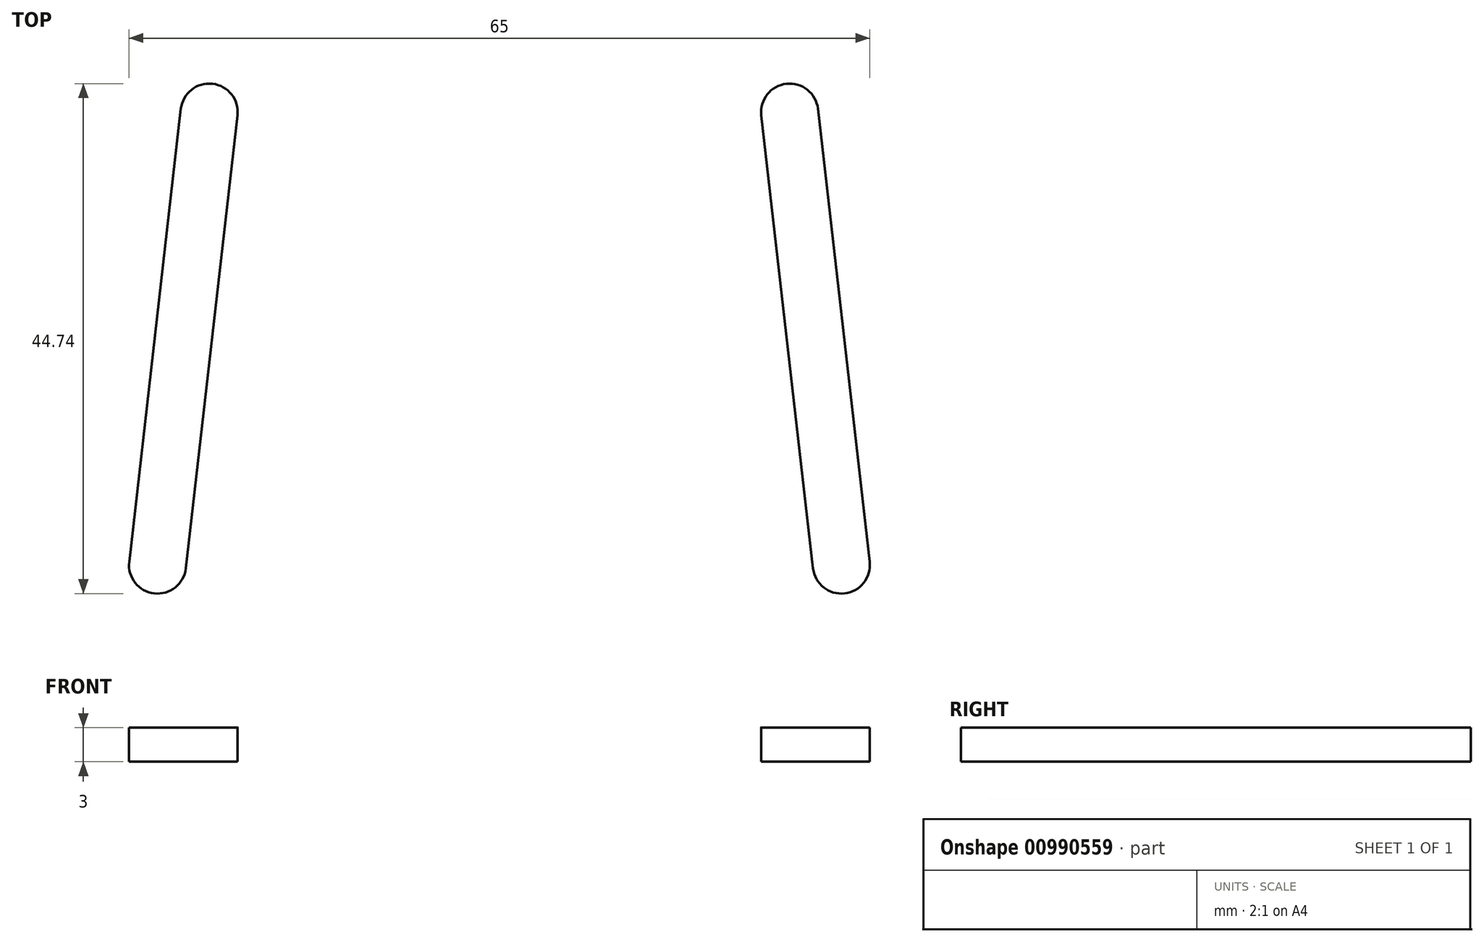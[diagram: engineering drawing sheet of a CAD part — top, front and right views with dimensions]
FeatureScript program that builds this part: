
annotation { "Feature Type Name" : "Feature", "Feature Type Description" : "" }
export const myFeature = defineFeature(function(context is Context, id is Id, definition is map)
    precondition{}
    {
        {
            var Q0;
            Q0=qCreatedBy(makeId("Top.planeOp"),FACE);
            var sketch = newSketch(context, id + "F0", { "sketchPlane" : qUnion([Q0])});
            skLineSegment(sketch, "E0.bottom", {"start": v(0, 0) * mm, "end": v(40, 0) * mm});
            skLineSegment(sketch, "E0.top", {"start": v(0, 100) * mm, "end": v(40, 100) * mm});
            skLineSegment(sketch, "E0.left", {"start": v(0, 0) * mm, "end": v(0, 100) * mm});
            skLineSegment(sketch, "E0.right", {"start": v(40, 0) * mm, "end": v(40, 100) * mm});
            skSolve(sketch);
        }
        {
            var Q0;
            Q0=makeQuery(id+"F0.imprint","IMPRINT",FACE,{"disambiguationData":[TD([[makeQuery(id+"F0.imprint","IMPRINT",EDGE,{"derivedFrom":sQuery(id+"F0.wireOp",EDGE,"E0.bottom")}),1.0]])]});
            extrude(context, id + "F1", {"entities" : qUnion([Q0]), "depth" : 3 * mm, "offsetDistance" : 25 * mm});
        }
        {
            var Q0;
            Q0=makeQuery(id+"F1.opExtrude","CAP_FACE",FACE,{"disambiguationData":[OSD([sQuery(id+"F0.wireOp",EDGE,"E0.bottom"),sQuery(id+"F0.wireOp",EDGE,"E0.top"),sQuery(id+"F0.wireOp",EDGE,"E0.left"),sQuery(id+"F0.wireOp",EDGE,"E0.right")])],"isStart":false});
            var sketch = newSketch(context, id + "F2", { "sketchPlane" : qUnion([Q0])});
            skSolve(sketch);
        }
        {
            var Q0;
            Q0=makeQuery(id+"F2.imprint","IMPRINT",FACE,{"disambiguationData":[TD([[makeQuery(id+"F2.imprint","IMPRINT",EDGE,{"derivedFrom":makeQuery(id+"F1.opExtrude","CAP_EDGE",EDGE,{"disambiguationData":[OSD([sQuery(id+"F0.wireOp",EDGE,"E0.bottom")])],"isStart":false})}),1.0]])]});
            var sketch = newSketch(context, id + "F3", { "sketchPlane" : qUnion([Q0])});
            skLineSegment(sketch, "E1", {"start": v(20, 50) * mm, "end": v(20, 25) * mm});
            skSolve(sketch);
        }
        {
            var Q0;
            Q0=sQuery(id+"F3.wireOp",VERTEX,"E1.start");
            var Q1;
            Q1=sQuery(id+"F3.wireOp",VERTEX,"E1.end");
            var Q2;
            Q2=makeQuery(id+"F1.opExtrude","SWEPT_BODY",BODY,{"disambiguationData":[OSD([sQuery(id+"F0.wireOp",EDGE,"E0.bottom"),sQuery(id+"F0.wireOp",EDGE,"E0.top"),sQuery(id+"F0.wireOp",EDGE,"E0.left"),sQuery(id+"F0.wireOp",EDGE,"E0.right")])]});
            hole(context, id + "F4", {"style" : HoleStyle.SIMPLE, "endStyle" : HoleEndStyle.THROUGH, "holeDiameter" : 3 * mm, "majorDiameter" : 5 * mm, "isTappedThrough" : true, "tappedDepth" : 12 * mm, "tapClearance" : 3, "locations" : qUnion([Q0, Q1]), "scope" : qUnion([Q2])});
        }
        {
            var Q0;
            Q0=makeQuery(id+"F2.imprint","IMPRINT",FACE,{"disambiguationData":[TD([[makeQuery(id+"F2.imprint","IMPRINT",EDGE,{"derivedFrom":makeQuery(id+"F1.opExtrude","CAP_EDGE",EDGE,{"disambiguationData":[OSD([sQuery(id+"F0.wireOp",EDGE,"E0.bottom")])],"isStart":false})}),1.0]])]});
            var sketch = newSketch(context, id + "F5", { "sketchPlane" : qUnion([Q0])});
            skLineSegment(sketch, "E2", {"start": v(30, 20) * mm, "end": v(25.46, 59.74) * mm});
            skSolve(sketch);
        }
        {
            var Q0;
            Q0=makeQuery(id+"F5.imprint","IMPRINT",FACE,{"disambiguationData":[TD([[makeQuery(id+"F5.imprint","IMPRINT",EDGE,{"derivedFrom":makeQuery(id+"F2.imprint","IMPRINT",EDGE,{"derivedFrom":makeQuery(id+"F1.opExtrude","CAP_EDGE",EDGE,{"disambiguationData":[OSD([sQuery(id+"F0.wireOp",EDGE,"E0.bottom")])],"isStart":false})})}),1.0]])]});
            var sketch = newSketch(context, id + "F6", { "sketchPlane" : qUnion([Q0])});
            skLineSegment(sketch, "E3.JWB.JWB", {"start": v(30, 20) * mm, "end": v(25.46, 59.74) * mm, "construction": true});
            skArc(sketch, "E3.0.startCap", {"start": v(32.48, 20.28) * mm, "mid": v(30.28, 17.52) * mm, "end": v(27.52, 19.72) * mm});
            skArc(sketch, "E3.0.endCap", {"start": v(22.98, 59.46) * mm, "mid": v(25.18, 62.23) * mm, "end": v(27.95, 60.03) * mm});
            skLineSegment(sketch, "E3.0.left", {"start": v(27.52, 19.72) * mm, "end": v(22.98, 59.46) * mm});
            skLineSegment(sketch, "E3.0.right", {"start": v(32.48, 20.28) * mm, "end": v(27.95, 60.03) * mm});
            skSolve(sketch);
        }
        {
            var Q0;
            Q0=makeQuery(id+"F6.imprint","IMPRINT",FACE,{"disambiguationData":[TD([[makeQuery(id+"F6.imprint","IMPRINT",EDGE,{"derivedFrom":sQuery(id+"F6.wireOp",EDGE,"E3.0.startCap")}),-1.0]])]});
            extrude(context, id + "F7", {"entities" : qUnion([Q0]), "operationType" : NewBodyOperationType.REMOVE, "oppositeDirection" : true, "depth" : 41.6 * mm, "offsetDistance" : 25 * mm});
        }
        {
            var Q0;
            Q0=makeQuery(id+"F1.opExtrude","SWEPT_BODY",BODY,{"disambiguationData":[OSD([sQuery(id+"F0.wireOp",EDGE,"E0.bottom"),sQuery(id+"F0.wireOp",EDGE,"E0.top"),sQuery(id+"F0.wireOp",EDGE,"E0.left"),sQuery(id+"F0.wireOp",EDGE,"E0.right")])]});
            var Q1;
            Q1=qCreatedBy(makeId("Right.planeOp"),FACE);
            mirror(context, id + "F8", {"operationType" : NewBodyOperationType.ADD, "entities" : qUnion([Q0]), "mirrorPlane" : qUnion([Q1])});
        }
    });
